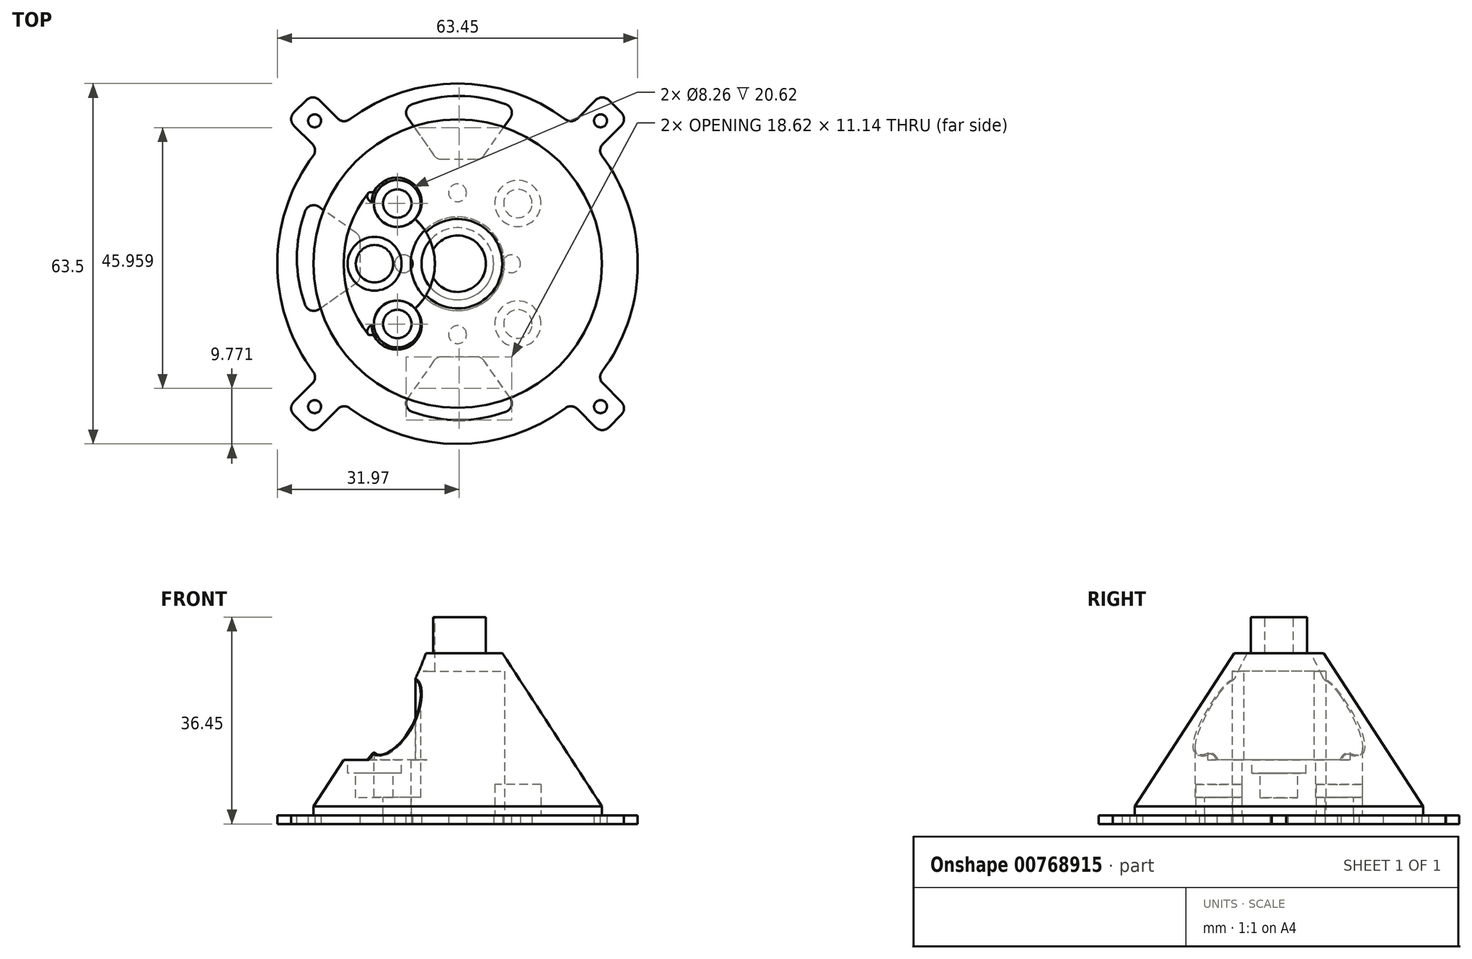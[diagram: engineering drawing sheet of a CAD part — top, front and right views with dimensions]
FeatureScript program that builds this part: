
annotation { "Feature Type Name" : "Feature", "Feature Type Description" : "" }
export const myFeature = defineFeature(function(context is Context, id is Id, definition is map)
    precondition{}
    {
        {
            var Q0;
            Q0=qCreatedBy(makeId("Top.planeOp"),FACE);
            var sketch = newSketch(context, id + "F0", { "sketchPlane" : qUnion([Q0])});
            skCircle(sketch, "E0", {"center": v(-0.25, -1) * mm, "radius": 6.35 * mm});
            skArc(sketch, "E1", {"start": v(-31.97, -2.27) * mm, "mid": v(-0.25, -32.75) * mm, "end": v(31.48, -2.27) * mm});
            skArc(sketch, "E2", {"start": v(-66.24, 8.52) * mm, "mid": v(-66.7, 4.4) * mm, "end": v(-66.91, 0.27) * mm});
            skArc(sketch, "E3", {"start": v(-82.25, 8.52) * mm, "mid": v(-82.8, -1) * mm, "end": v(-82.25, -10.53) * mm});
            skCircle(sketch, "E4", {"center": v(-0.25, -1) * mm, "radius": 15.01 * mm, "construction": true});
            skLineSegment(sketch, "E5", {"start": v(-0.25, -1) * mm, "end": v(-82.8, -1) * mm, "construction": true});
            skLineSegment(sketch, "E6", {"start": v(-0.25, -1) * mm, "end": v(82.3, -1) * mm, "construction": true});
            skLineSegment(sketch, "E7", {"start": v(-66.91, 0.27) * mm, "end": v(-31.97, 0.27) * mm});
            skLineSegment(sketch, "E8", {"start": v(-66.91, -2.27) * mm, "end": v(-31.97, -2.27) * mm});
            skLineSegment(sketch, "E9", {"start": v(-82.25, 8.52) * mm, "end": v(-66.24, 8.52) * mm});
            skLineSegment(sketch, "E10", {"start": v(-82.25, -10.53) * mm, "end": v(-66.24, -10.53) * mm});
            skLineSegment(sketch, "E11", {"start": v(31.48, 0.27) * mm, "end": v(66.41, 0.27) * mm});
            skLineSegment(sketch, "E12", {"start": v(31.48, -2.27) * mm, "end": v(66.41, -2.27) * mm});
            skLineSegment(sketch, "E13", {"start": v(65.74, 8.52) * mm, "end": v(81.75, 8.52) * mm});
            skLineSegment(sketch, "E14", {"start": v(65.74, -10.53) * mm, "end": v(81.75, -10.53) * mm});
            skLineSegment(sketch, "E15", {"start": v(-0.25, -1) * mm, "end": v(-0.25, 65.67) * mm, "construction": true});
            skCircle(sketch, "E16", {"center": v(-10.86, 9.61) * mm, "radius": 2.5 * mm});
            skCircle(sketch, "E17", {"center": v(10.37, 9.61) * mm, "radius": 2.5 * mm});
            skCircle(sketch, "E18", {"center": v(-10.86, -11.62) * mm, "radius": 2.5 * mm});
            skCircle(sketch, "E19", {"center": v(10.37, -11.62) * mm, "radius": 2.5 * mm});
            skLineSegment(sketch, "E20", {"start": v(-27.98, 26.72) * mm, "end": v(10.37, -11.62) * mm, "construction": true});
            skLineSegment(sketch, "E21", {"start": v(10.37, 9.61) * mm, "end": v(-10.86, -11.62) * mm, "construction": true});
            skArc(sketch, "E22.trimOffspring", {"start": v(81.75, -10.53) * mm, "mid": v(82.3, -1) * mm, "end": v(81.75, 8.52) * mm});
            skArc(sketch, "E23.trimOffspring", {"start": v(65.74, -10.53) * mm, "mid": v(66.2, -6.41) * mm, "end": v(66.41, -2.27) * mm});
            skArc(sketch, "E24.trimOffspring", {"start": v(-66.24, -10.53) * mm, "mid": v(66.25, 3.77) * mm, "end": v(-66.92, -1) * mm, "construction": true});
            skArc(sketch, "E25.trimOffspring", {"start": v(-66.91, -2.27) * mm, "mid": v(-66.7, -6.41) * mm, "end": v(-66.24, -10.53) * mm});
            skArc(sketch, "E26.trimOffspring", {"start": v(31.48, 0.27) * mm, "mid": v(-0.25, 30.75) * mm, "end": v(-31.97, 0.27) * mm});
            skArc(sketch, "E27.trimOffspring", {"start": v(66.43, -1) * mm, "mid": v(66.25, 3.77) * mm, "end": v(65.74, 8.52) * mm, "construction": true});
            skArc(sketch, "E28.trimOffspring", {"start": v(66.41, 0.27) * mm, "mid": v(66.2, 4.4) * mm, "end": v(65.74, 8.52) * mm});
            skArc(sketch, "E29", {"start": v(-31.97, -2.27) * mm, "mid": v(-32, -1) * mm, "end": v(-31.97, 0.27) * mm});
            skArc(sketch, "E30", {"start": v(31.48, -2.27) * mm, "mid": v(31.5, -1) * mm, "end": v(31.48, 0.27) * mm});
            skCircle(sketch, "E31", {"center": v(-76.45, -1) * mm, "radius": 3.24 * mm});
            skCircle(sketch, "E32.MirrorC", {"center": v(75.95, -1) * mm, "radius": 3.24 * mm});
            skCircle(sketch, "E33", {"center": v(-9.75, -1) * mm, "radius": 1.57 * mm});
            skCircle(sketch, "E34", {"center": v(9.25, -1) * mm, "radius": 1.57 * mm});
            skCircle(sketch, "E35", {"center": v(-0.25, 11.5) * mm, "radius": 1.57 * mm});
            skCircle(sketch, "E36", {"center": v(-0.25, -13.5) * mm, "radius": 1.57 * mm});
            skCircle(sketch, "E37", {"center": v(-0.25, -1) * mm, "radius": 9.5 * mm, "construction": true});
            skCircle(sketch, "E38", {"center": v(-0.25, -1) * mm, "radius": 12.5 * mm, "construction": true});
            skLineSegment(sketch, "E39", {"start": v(-66.91, 0.27) * mm, "end": v(-66.91, -2.27) * mm});
            skLineSegment(sketch, "E40", {"start": v(66.41, 0.27) * mm, "end": v(66.41, -2.27) * mm});
            skLineSegment(sketch, "E41.bottom", {"start": v(-31.97, -2.27) * mm, "end": v(-62.47, -2.27) * mm});
            skLineSegment(sketch, "E41.top", {"start": v(-31.97, 0.27) * mm, "end": v(-62.47, 0.27) * mm});
            skLineSegment(sketch, "E41.right", {"start": v(-62.47, -2.27) * mm, "end": v(-62.47, 0.27) * mm});
            skLineSegment(sketch, "E42.bottom", {"start": v(31.48, -2.27) * mm, "end": v(61.97, -2.27) * mm});
            skLineSegment(sketch, "E42.top", {"start": v(31.48, 0.27) * mm, "end": v(61.97, 0.27) * mm});
            skLineSegment(sketch, "E42.right", {"start": v(61.97, -2.27) * mm, "end": v(61.97, 0.27) * mm});
            skCircle(sketch, "E43", {"center": v(-0.25, -1) * mm, "radius": 62.23 * mm, "construction": true});
            skLineSegment(sketch, "E44.bottom", {"start": v(-31.97, 0.27) * mm, "end": v(-28.8, 0.27) * mm});
            skLineSegment(sketch, "E44.top", {"start": v(-31.97, -2.27) * mm, "end": v(-28.8, -2.27) * mm});
            skLineSegment(sketch, "E44.left", {"start": v(-31.97, 0.27) * mm, "end": v(-31.97, -2.27) * mm});
            skLineSegment(sketch, "E44.right", {"start": v(-28.8, 0.27) * mm, "end": v(-28.8, -2.27) * mm});
            skLineSegment(sketch, "E45.bottom", {"start": v(31.48, 0.27) * mm, "end": v(28.3, 0.27) * mm});
            skLineSegment(sketch, "E45.top", {"start": v(31.48, -2.27) * mm, "end": v(28.3, -2.27) * mm});
            skLineSegment(sketch, "E45.left", {"start": v(31.48, 0.27) * mm, "end": v(31.48, -2.27) * mm});
            skLineSegment(sketch, "E45.right", {"start": v(28.3, 0.27) * mm, "end": v(28.3, -2.27) * mm});
            skLineSegment(sketch, "E46", {"start": v(-20.34, 23.58) * mm, "end": v(-25.73, 28.97) * mm});
            skLineSegment(sketch, "E47", {"start": v(-25.73, 28.97) * mm, "end": v(-30.22, 24.48) * mm});
            skLineSegment(sketch, "E48", {"start": v(-30.22, 24.48) * mm, "end": v(-24.83, 19.09) * mm});
            skCircle(sketch, "E49", {"center": v(-25.43, 24.17) * mm, "radius": 1.14 * mm});
            skPoint(sketch, "E50.center", {"position": v(0, 0) * mm});
            skLineSegment(sketch, "E51.1.0", {"start": v(-25.73, -30.98) * mm, "end": v(-20.34, -25.59) * mm});
            skLineSegment(sketch, "E51.1.1", {"start": v(-24.83, -21.1) * mm, "end": v(-30.22, -26.49) * mm});
            skLineSegment(sketch, "E51.1.2", {"start": v(-30.22, -26.49) * mm, "end": v(-25.73, -30.98) * mm});
            skCircle(sketch, "E51.1.3", {"center": v(-25.43, -26.18) * mm, "radius": 1.14 * mm});
            skLineSegment(sketch, "E51.2.0", {"start": v(29.72, -26.49) * mm, "end": v(24.33, -21.1) * mm});
            skLineSegment(sketch, "E51.2.1", {"start": v(19.84, -25.59) * mm, "end": v(25.23, -30.98) * mm});
            skLineSegment(sketch, "E51.2.2", {"start": v(25.23, -30.98) * mm, "end": v(29.72, -26.49) * mm});
            skCircle(sketch, "E51.2.3", {"center": v(24.93, -26.18) * mm, "radius": 1.14 * mm});
            skLineSegment(sketch, "E51.3.0", {"start": v(25.23, 28.97) * mm, "end": v(19.84, 23.58) * mm});
            skLineSegment(sketch, "E51.3.1", {"start": v(24.33, 19.09) * mm, "end": v(29.72, 24.48) * mm});
            skLineSegment(sketch, "E51.3.2", {"start": v(29.72, 24.48) * mm, "end": v(25.23, 28.97) * mm});
            skCircle(sketch, "E51.3.3", {"center": v(24.93, 24.17) * mm, "radius": 1.14 * mm});
            skSolve(sketch);
        }
        {
            var Q0;
            Q0=makeQuery(id+"F0.imprint","IMPRINT",FACE,{"disambiguationData":[TD([[makeQuery(id+"F0.imprint","IMPRINT",EDGE,{"derivedFrom":sQuery(id+"F0.wireOp",EDGE,"E0")}),-1.0]])]});
            var Q1;
            Q1=makeQuery(id+"F0.imprint","IMPRINT",FACE,{"disambiguationData":[TD([[makeQuery(id+"F0.imprint","IMPRINT",EDGE,{"derivedFrom":sQuery(id+"F0.wireOp",EDGE,"E44.bottom")}),-1.0]])]});
            var Q2;
            Q2=makeQuery(id+"F0.imprint","IMPRINT",FACE,{"disambiguationData":[TD([[makeQuery(id+"F0.imprint","IMPRINT",EDGE,{"derivedFrom":sQuery(id+"F0.wireOp",EDGE,"E45.bottom")}),1.0]])]});
            var Q3;
            {var subQ1=sQuery(id+"F0.wireOp",EDGE,"E46");Q3=makeQuery(id+"F0.imprint","IMPRINT",FACE,{"disambiguationData":[TD([[makeQuery(id+"F0.imprint","IMPRINT",EDGE,{"derivedFrom":subQ1}),1.0]])]});}
            var Q4;
            {var subQ1=sQuery(id+"F0.wireOp",EDGE,"E51.3.0");Q4=makeQuery(id+"F0.imprint","IMPRINT",FACE,{"disambiguationData":[TD([[makeQuery(id+"F0.imprint","IMPRINT",EDGE,{"derivedFrom":subQ1}),1.0]])]});}
            var Q5;
            {var subQ1=sQuery(id+"F0.wireOp",EDGE,"E51.2.0");Q5=makeQuery(id+"F0.imprint","IMPRINT",FACE,{"disambiguationData":[TD([[makeQuery(id+"F0.imprint","IMPRINT",EDGE,{"derivedFrom":subQ1}),1.0]])]});}
            var Q6;
            {var subQ1=sQuery(id+"F0.wireOp",EDGE,"E51.1.0");Q6=makeQuery(id+"F0.imprint","IMPRINT",FACE,{"disambiguationData":[TD([[makeQuery(id+"F0.imprint","IMPRINT",EDGE,{"derivedFrom":subQ1}),1.0]])]});}
            extrude(context, id + "F1", {"entities" : qUnion([Q0, Q1, Q2, Q3, Q4, Q5, Q6]), "depth" : 1.52 * mm, "offsetDistance" : 25.4 * mm});
        }
        {
            var Q0;
            Q0=makeQuery(id+"F1.opExtrude","CAP_FACE",FACE,{"disambiguationData":[OSD([sQuery(id+"F0.wireOp",EDGE,"E0"),sQuery(id+"F0.wireOp",EDGE,"E1"),sQuery(id+"F0.wireOp",EDGE,"E16"),sQuery(id+"F0.wireOp",EDGE,"E17"),sQuery(id+"F0.wireOp",EDGE,"E18"),sQuery(id+"F0.wireOp",EDGE,"E19"),sQuery(id+"F0.wireOp",EDGE,"E26.trimOffspring"),sQuery(id+"F0.wireOp",EDGE,"E33"),sQuery(id+"F0.wireOp",EDGE,"E34"),sQuery(id+"F0.wireOp",EDGE,"E35"),sQuery(id+"F0.wireOp",EDGE,"E36"),sQuery(id+"F0.wireOp",EDGE,"E44.left"),sQuery(id+"F0.wireOp",EDGE,"E45.left")])],"isStart":false});
            var sketch = newSketch(context, id + "F2", { "sketchPlane" : qUnion([Q0])});
            skLineSegment(sketch, "E52", {"start": v(-4.4, -18.09) * mm, "end": v(-9.03, -24.68) * mm});
            skLineSegment(sketch, "E53", {"start": v(9.03, -24.68) * mm, "end": v(4.4, -18.09) * mm});
            skLineSegment(sketch, "E54", {"start": v(3.1, -17.41) * mm, "end": v(-3.1, -17.41) * mm});
            skArc(sketch, "E55", {"start": v(-8.27, -27.08) * mm, "mid": v(0, -28.55) * mm, "end": v(8.27, -27.08) * mm});
            skPoint(sketch, "E56.visualSharp", {"position": v(-3.94, -17.41) * mm});
            skArc(sketch, "E56.filletArc", {"start": v(-3.1, -17.41) * mm, "mid": v(-3.84, -17.59) * mm, "end": v(-4.4, -18.09) * mm});
            skPoint(sketch, "E57.visualSharp", {"position": v(-10.16, -26.3) * mm});
            skArc(sketch, "E57.filletArc", {"start": v(-9.03, -24.68) * mm, "mid": v(-9.24, -26.07) * mm, "end": v(-8.27, -27.08) * mm});
            skPoint(sketch, "E58.visualSharp", {"position": v(10.16, -26.3) * mm});
            skArc(sketch, "E58.filletArc", {"start": v(8.27, -27.08) * mm, "mid": v(9.24, -26.07) * mm, "end": v(9.03, -24.68) * mm});
            skPoint(sketch, "E59.visualSharp", {"position": v(3.94, -17.41) * mm});
            skArc(sketch, "E59.filletArc", {"start": v(4.4, -18.09) * mm, "mid": v(3.84, -17.59) * mm, "end": v(3.1, -17.41) * mm});
            skPoint(sketch, "E60.1.0", {"position": v(-17.41, 3.94) * mm});
            skLineSegment(sketch, "E60.1.1", {"start": v(-17.41, -3.1) * mm, "end": v(-17.41, 3.1) * mm});
            skArc(sketch, "E60.1.2", {"start": v(-27.08, 8.27) * mm, "mid": v(-28.55, 0) * mm, "end": v(-27.08, -8.27) * mm});
            skPoint(sketch, "E60.1.3", {"position": v(-26.3, 10.16) * mm});
            skLineSegment(sketch, "E60.1.4", {"start": v(-24.68, -9.03) * mm, "end": v(-18.09, -4.4) * mm});
            skPoint(sketch, "E60.1.5", {"position": v(-26.3, -10.16) * mm});
            skPoint(sketch, "E60.1.6", {"position": v(-17.41, -3.94) * mm});
            skLineSegment(sketch, "E60.1.7", {"start": v(-18.09, 4.4) * mm, "end": v(-24.68, 9.03) * mm});
            skArc(sketch, "E60.1.8", {"start": v(-27.08, -8.27) * mm, "mid": v(-26.07, -9.24) * mm, "end": v(-24.68, -9.03) * mm});
            skArc(sketch, "E60.1.9", {"start": v(-24.68, 9.03) * mm, "mid": v(-26.07, 9.24) * mm, "end": v(-27.08, 8.27) * mm});
            skArc(sketch, "E60.1.10", {"start": v(-18.09, -4.4) * mm, "mid": v(-17.59, -3.84) * mm, "end": v(-17.41, -3.1) * mm});
            skArc(sketch, "E60.1.11", {"start": v(-17.41, 3.1) * mm, "mid": v(-17.59, 3.84) * mm, "end": v(-18.09, 4.4) * mm});
            skPoint(sketch, "E60.2.0", {"position": v(3.94, 17.41) * mm});
            skLineSegment(sketch, "E60.2.1", {"start": v(-3.1, 17.41) * mm, "end": v(3.1, 17.41) * mm});
            skArc(sketch, "E60.2.2", {"start": v(8.27, 27.08) * mm, "mid": v(0, 28.55) * mm, "end": v(-8.27, 27.08) * mm});
            skPoint(sketch, "E60.2.3", {"position": v(10.16, 26.3) * mm});
            skLineSegment(sketch, "E60.2.4", {"start": v(-9.03, 24.68) * mm, "end": v(-4.4, 18.09) * mm});
            skPoint(sketch, "E60.2.5", {"position": v(-10.16, 26.3) * mm});
            skPoint(sketch, "E60.2.6", {"position": v(-3.94, 17.41) * mm});
            skLineSegment(sketch, "E60.2.7", {"start": v(4.4, 18.09) * mm, "end": v(9.03, 24.68) * mm});
            skArc(sketch, "E60.2.8", {"start": v(-8.27, 27.08) * mm, "mid": v(-9.24, 26.07) * mm, "end": v(-9.03, 24.68) * mm});
            skArc(sketch, "E60.2.9", {"start": v(9.03, 24.68) * mm, "mid": v(9.24, 26.07) * mm, "end": v(8.27, 27.08) * mm});
            skArc(sketch, "E60.2.10", {"start": v(-4.4, 18.09) * mm, "mid": v(-3.84, 17.59) * mm, "end": v(-3.1, 17.41) * mm});
            skArc(sketch, "E60.2.11", {"start": v(3.1, 17.41) * mm, "mid": v(3.84, 17.59) * mm, "end": v(4.4, 18.09) * mm});
            skPoint(sketch, "E60.center", {"position": v(0, 0) * mm});
            skLineSegment(sketch, "E60.anchor1", {"start": v(0, 0) * mm, "end": v(-10.16, -26.3) * mm, "construction": true});
            skLineSegment(sketch, "E60.anchor2", {"start": v(0, 0) * mm, "end": v(10.16, 26.3) * mm, "construction": true});
            skSolve(sketch);
        }
        {
            var Q0;
            Q0 = qSketchRegion(id + "F2", true);
            extrude(context, id + "F3", {"entities" : qUnion([Q0]), "operationType" : NewBodyOperationType.REMOVE, "endBound" : BoundingType.THROUGH_ALL, "oppositeDirection" : true, "depth" : 25.4 * mm, "offsetDistance" : 25.4 * mm});
        }
        {
            var Q0;
            Q0=makeQuery(id+"F1.opExtrude","SWEPT_EDGE",EDGE,{"disambiguationData":[OSD([sQuery(id+"F0.wireOp",EDGE,"E26.trimOffspring"),sQuery(id+"F0.wireOp",EDGE,"E48")])]});
            var Q1;
            Q1=makeQuery(id+"F1.opExtrude","SWEPT_EDGE",EDGE,{"disambiguationData":[OSD([sQuery(id+"F0.wireOp",EDGE,"E47"),sQuery(id+"F0.wireOp",EDGE,"E48")])]});
            var Q2;
            Q2=makeQuery(id+"F1.opExtrude","SWEPT_EDGE",EDGE,{"disambiguationData":[OSD([sQuery(id+"F0.wireOp",EDGE,"E46"),sQuery(id+"F0.wireOp",EDGE,"E47")])]});
            var Q3;
            Q3=makeQuery(id+"F1.opExtrude","SWEPT_EDGE",EDGE,{"disambiguationData":[OSD([sQuery(id+"F0.wireOp",EDGE,"E26.trimOffspring"),sQuery(id+"F0.wireOp",EDGE,"E46")])]});
            var Q4;
            Q4=makeQuery(id+"F1.opExtrude","SWEPT_EDGE",EDGE,{"disambiguationData":[OSD([sQuery(id+"F0.wireOp",EDGE,"E26.trimOffspring"),sQuery(id+"F0.wireOp",EDGE,"E51.3.0")])]});
            var Q5;
            Q5=makeQuery(id+"F1.opExtrude","SWEPT_EDGE",EDGE,{"disambiguationData":[OSD([sQuery(id+"F0.wireOp",EDGE,"E51.3.0"),sQuery(id+"F0.wireOp",EDGE,"E51.3.2")])]});
            var Q6;
            Q6=makeQuery(id+"F1.opExtrude","SWEPT_EDGE",EDGE,{"disambiguationData":[OSD([sQuery(id+"F0.wireOp",EDGE,"E51.3.1"),sQuery(id+"F0.wireOp",EDGE,"E51.3.2")])]});
            var Q7;
            Q7=makeQuery(id+"F1.opExtrude","SWEPT_EDGE",EDGE,{"disambiguationData":[OSD([sQuery(id+"F0.wireOp",EDGE,"E26.trimOffspring"),sQuery(id+"F0.wireOp",EDGE,"E51.3.1")])]});
            var Q8;
            Q8=makeQuery(id+"F1.opExtrude","SWEPT_EDGE",EDGE,{"disambiguationData":[OSD([sQuery(id+"F0.wireOp",EDGE,"E1"),sQuery(id+"F0.wireOp",EDGE,"E51.2.0")])]});
            var Q9;
            Q9=makeQuery(id+"F1.opExtrude","SWEPT_EDGE",EDGE,{"disambiguationData":[OSD([sQuery(id+"F0.wireOp",EDGE,"E51.2.0"),sQuery(id+"F0.wireOp",EDGE,"E51.2.2")])]});
            var Q10;
            Q10=makeQuery(id+"F1.opExtrude","SWEPT_EDGE",EDGE,{"disambiguationData":[OSD([sQuery(id+"F0.wireOp",EDGE,"E51.2.1"),sQuery(id+"F0.wireOp",EDGE,"E51.2.2")])]});
            var Q11;
            Q11=makeQuery(id+"F1.opExtrude","SWEPT_EDGE",EDGE,{"disambiguationData":[OSD([sQuery(id+"F0.wireOp",EDGE,"E1"),sQuery(id+"F0.wireOp",EDGE,"E51.2.1")])]});
            var Q12;
            Q12=makeQuery(id+"F1.opExtrude","SWEPT_EDGE",EDGE,{"disambiguationData":[OSD([sQuery(id+"F0.wireOp",EDGE,"E1"),sQuery(id+"F0.wireOp",EDGE,"E51.1.0")])]});
            var Q13;
            Q13=makeQuery(id+"F1.opExtrude","SWEPT_EDGE",EDGE,{"disambiguationData":[OSD([sQuery(id+"F0.wireOp",EDGE,"E51.1.0"),sQuery(id+"F0.wireOp",EDGE,"E51.1.2")])]});
            var Q14;
            Q14=makeQuery(id+"F1.opExtrude","SWEPT_EDGE",EDGE,{"disambiguationData":[OSD([sQuery(id+"F0.wireOp",EDGE,"E51.1.1"),sQuery(id+"F0.wireOp",EDGE,"E51.1.2")])]});
            var Q15;
            Q15=makeQuery(id+"F1.opExtrude","SWEPT_EDGE",EDGE,{"disambiguationData":[OSD([sQuery(id+"F0.wireOp",EDGE,"E1"),sQuery(id+"F0.wireOp",EDGE,"E51.1.1")])]});
            fillet(context, id + "F4", {"entities" : qUnion([Q0, Q1, Q2, Q3, Q4, Q5, Q6, Q7, Q8, Q9, Q10, Q11, Q12, Q13, Q14, Q15]), "radius" : 1.59 * mm, "tangentPropagation" : true, "allowEdgeOverflow" : false});
        }
        {
            var Q0;
            Q0=makeQuery(id+"F1.opExtrude","CAP_FACE",FACE,{"disambiguationData":[OSD([sQuery(id+"F0.wireOp",EDGE,"E0"),sQuery(id+"F0.wireOp",EDGE,"E1"),sQuery(id+"F0.wireOp",EDGE,"E16"),sQuery(id+"F0.wireOp",EDGE,"E17"),sQuery(id+"F0.wireOp",EDGE,"E18"),sQuery(id+"F0.wireOp",EDGE,"E19"),sQuery(id+"F0.wireOp",EDGE,"E26.trimOffspring"),sQuery(id+"F0.wireOp",EDGE,"E33"),sQuery(id+"F0.wireOp",EDGE,"E34"),sQuery(id+"F0.wireOp",EDGE,"E35"),sQuery(id+"F0.wireOp",EDGE,"E36"),sQuery(id+"F0.wireOp",EDGE,"E44.left"),sQuery(id+"F0.wireOp",EDGE,"E45.left"),sQuery(id+"F0.wireOp",EDGE,"E46"),sQuery(id+"F0.wireOp",EDGE,"E47"),sQuery(id+"F0.wireOp",EDGE,"E48"),sQuery(id+"F0.wireOp",EDGE,"E49"),sQuery(id+"F0.wireOp",EDGE,"E51.1.0"),sQuery(id+"F0.wireOp",EDGE,"E51.1.1"),sQuery(id+"F0.wireOp",EDGE,"E51.1.2"),sQuery(id+"F0.wireOp",EDGE,"E51.1.3"),sQuery(id+"F0.wireOp",EDGE,"E51.2.0"),sQuery(id+"F0.wireOp",EDGE,"E51.2.1"),sQuery(id+"F0.wireOp",EDGE,"E51.2.2"),sQuery(id+"F0.wireOp",EDGE,"E51.2.3"),sQuery(id+"F0.wireOp",EDGE,"E51.3.0"),sQuery(id+"F0.wireOp",EDGE,"E51.3.1"),sQuery(id+"F0.wireOp",EDGE,"E51.3.2"),sQuery(id+"F0.wireOp",EDGE,"E51.3.3")])],"isStart":false});
            var sketch = newSketch(context, id + "F5", { "sketchPlane" : qUnion([Q0])});
            skCircle(sketch, "E61", {"center": v(-0.25, -1) * mm, "radius": 25.4 * mm});
            skSolve(sketch);
        }
        {
            var Q0;
            Q0 = qSketchRegion(id + "F5", true);
            extrude(context, id + "F6", {"entities" : qUnion([Q0]), "depth" : 1.59 * mm, "offsetDistance" : 25.4 * mm});
        }
        {
            var Q0;
            Q0=makeQuery(id+"F6.opExtrude","CAP_FACE",FACE,{"disambiguationData":[OSD([sQuery(id+"F5.wireOp",EDGE,"E61")])],"isStart":false});
            extrude(context, id + "F7", {"entities" : qUnion([Q0]), "operationType" : NewBodyOperationType.ADD, "depth" : 26.99 * mm, "offsetDistance" : 25.4 * mm, "hasDraft" : true, "draftAngle" : 33 * degree, "draftPullDirection" : true});
        }
        {
            var Q0;
            Q0=makeQuery(id+"F7.opExtrude","CAP_FACE",FACE,{"disambiguationData":[OSD([sQuery(id+"F5.wireOp",EDGE,"E61")])],"isStart":false});
            var sketch = newSketch(context, id + "F8", { "sketchPlane" : qUnion([Q0])});
            skCircle(sketch, "E62", {"center": v(-0.25, -1) * mm, "radius": 4.98 * mm});
            skSolve(sketch);
        }
        {
            var Q0;
            Q0=makeQuery(id+"F8.imprint","IMPRINT",FACE,{"disambiguationData":[TD([[makeQuery(id+"F8.imprint","IMPRINT",EDGE,{"derivedFrom":sQuery(id+"F8.wireOp",EDGE,"E62")}),1.0]])]});
            extrude(context, id + "F9", {"entities" : qUnion([Q0]), "operationType" : NewBodyOperationType.ADD, "depth" : 6.35 * mm, "offsetDistance" : 25.4 * mm});
        }
        {
            var Q0;
            Q0=makeQuery(id+"F6.opExtrude","CAP_FACE",FACE,{"disambiguationData":[OSD([sQuery(id+"F5.wireOp",EDGE,"E61")])],"isStart":true});
            var sketch = newSketch(context, id + "F10", { "sketchPlane" : qUnion([Q0])});
            skCircle(sketch, "E63", {"center": v(-0.25, 1) * mm, "radius": 8.26 * mm});
            skSolve(sketch);
        }
        {
            var Q0;
            Q0 = qSketchRegion(id + "F10", true);
            extrude(context, id + "F11", {"entities" : qUnion([Q0]), "operationType" : NewBodyOperationType.REMOVE, "oppositeDirection" : true, "depth" : 25.4 * mm, "offsetDistance" : 25.4 * mm});
        }
        {
            var Q0;
            Q0=makeQuery(id+"F7.opExtrude","CAP_FACE",FACE,{"disambiguationData":[OSD([sQuery(id+"F5.wireOp",EDGE,"E61")])],"isStart":false});
            var sketch = newSketch(context, id + "F12", { "sketchPlane" : qUnion([Q0])});
            skCircle(sketch, "E64", {"center": v(-14.87, -1) * mm, "radius": 10.63 * mm});
            skSolve(sketch);
        }
        {
            var Q0;
            Q0 = qSketchRegion(id + "F12", true);
            extrude(context, id + "F13", {"entities" : qUnion([Q0]), "operationType" : NewBodyOperationType.REMOVE, "oppositeDirection" : true, "depth" : 18.8 * mm, "offsetDistance" : 25.4 * mm, "hasSecondDirection" : true, "secondDirectionOppositeDirection" : false, "secondDirectionDepth" : 25.4 * mm});
        }
        {
            var Q0;
            Q0=makeQuery(id+"F13.boolean.opBoolean","COPY",FACE,{"derivedFrom":makeQuery(id+"F13.opExtrude","CAP_FACE",FACE,{"disambiguationData":[OSD([sQuery(id+"F5.wireOp",EDGE,"E61"),sQuery(id+"F12.wireOp",EDGE,"E64")])],"isStart":false})});
            var sketch = newSketch(context, id + "F14", { "sketchPlane" : qUnion([Q0])});
            skCircle(sketch, "E65", {"center": v(-14.87, -1) * mm, "radius": 4.74 * mm});
            skSolve(sketch);
        }
        {
            var Q0;
            Q0=makeQuery(id+"F14.imprint","IMPRINT",FACE,{"disambiguationData":[TD([[makeQuery(id+"F14.imprint","IMPRINT",EDGE,{"derivedFrom":sQuery(id+"F14.wireOp",EDGE,"E65")}),1.0]])]});
            extrude(context, id + "F15", {"entities" : qUnion([Q0]), "operationType" : NewBodyOperationType.REMOVE, "oppositeDirection" : true, "depth" : 2.38 * mm, "offsetDistance" : 25.4 * mm});
        }
        {
            var Q0;
            Q0=makeQuery(id+"F15.boolean.opBoolean","COPY",FACE,{"derivedFrom":makeQuery(id+"F15.opExtrude","CAP_FACE",FACE,{"disambiguationData":[OSD([sQuery(id+"F14.wireOp",EDGE,"E65")])],"isStart":false})});
            var sketch = newSketch(context, id + "F16", { "sketchPlane" : qUnion([Q0])});
            skCircle(sketch, "E66", {"center": v(-14.87, -1) * mm, "radius": 3.3 * mm});
            skSolve(sketch);
        }
        {
            var Q0;
            Q0=makeQuery(id+"F16.imprint","IMPRINT",FACE,{"disambiguationData":[TD([[makeQuery(id+"F16.imprint","IMPRINT",EDGE,{"derivedFrom":sQuery(id+"F16.wireOp",EDGE,"E66")}),1.0]])]});
            extrude(context, id + "F17", {"entities" : qUnion([Q0]), "operationType" : NewBodyOperationType.REMOVE, "oppositeDirection" : true, "depth" : 4.32 * mm, "offsetDistance" : 25.4 * mm});
        }
        {
            var Q0;
            Q0=makeQuery(id+"F1.opExtrude","CAP_FACE",FACE,{"disambiguationData":[OSD([sQuery(id+"F0.wireOp",EDGE,"E0"),sQuery(id+"F0.wireOp",EDGE,"E1"),sQuery(id+"F0.wireOp",EDGE,"E16"),sQuery(id+"F0.wireOp",EDGE,"E17"),sQuery(id+"F0.wireOp",EDGE,"E18"),sQuery(id+"F0.wireOp",EDGE,"E19"),sQuery(id+"F0.wireOp",EDGE,"E26.trimOffspring"),sQuery(id+"F0.wireOp",EDGE,"E33"),sQuery(id+"F0.wireOp",EDGE,"E34"),sQuery(id+"F0.wireOp",EDGE,"E35"),sQuery(id+"F0.wireOp",EDGE,"E36"),sQuery(id+"F0.wireOp",EDGE,"E44.left"),sQuery(id+"F0.wireOp",EDGE,"E45.left"),sQuery(id+"F0.wireOp",EDGE,"E46"),sQuery(id+"F0.wireOp",EDGE,"E47"),sQuery(id+"F0.wireOp",EDGE,"E48"),sQuery(id+"F0.wireOp",EDGE,"E49"),sQuery(id+"F0.wireOp",EDGE,"E51.1.0"),sQuery(id+"F0.wireOp",EDGE,"E51.1.1"),sQuery(id+"F0.wireOp",EDGE,"E51.1.2"),sQuery(id+"F0.wireOp",EDGE,"E51.1.3"),sQuery(id+"F0.wireOp",EDGE,"E51.2.0"),sQuery(id+"F0.wireOp",EDGE,"E51.2.1"),sQuery(id+"F0.wireOp",EDGE,"E51.2.2"),sQuery(id+"F0.wireOp",EDGE,"E51.2.3"),sQuery(id+"F0.wireOp",EDGE,"E51.3.0"),sQuery(id+"F0.wireOp",EDGE,"E51.3.1"),sQuery(id+"F0.wireOp",EDGE,"E51.3.2"),sQuery(id+"F0.wireOp",EDGE,"E51.3.3")])],"isStart":false});
            var sketch = newSketch(context, id + "F18", { "sketchPlane" : qUnion([Q0])});
            skCircle(sketch, "E67", {"center": v(10.37, -11.62) * mm, "radius": 4.06 * mm});
            skCircle(sketch, "E68", {"center": v(10.37, 9.61) * mm, "radius": 4.06 * mm});
            skSolve(sketch);
        }
        {
            var Q0;
            Q0 = qSketchRegion(id + "F18", true);
            extrude(context, id + "F19", {"entities" : qUnion([Q0]), "operationType" : NewBodyOperationType.REMOVE, "depth" : 5.46 * mm, "offsetDistance" : 25.4 * mm});
        }
        {
            var Q0;
            Q0=makeQuery(id+"F7.opExtrude","CAP_FACE",FACE,{"disambiguationData":[OSD([sQuery(id+"F5.wireOp",EDGE,"E61")])],"isStart":false});
            var sketch = newSketch(context, id + "F20", { "sketchPlane" : qUnion([Q0])});
            skCircle(sketch, "E69", {"center": v(-10.86, -11.62) * mm, "radius": 4.13 * mm});
            skCircle(sketch, "E70", {"center": v(-10.86, 9.61) * mm, "radius": 4.13 * mm});
            skSolve(sketch);
        }
        {
            var Q0;
            Q0 = qSketchRegion(id + "F20", true);
            var Q1;
            Q1=makeQuery(id+"F1.opExtrude","CAP_FACE",FACE,{"disambiguationData":[OSD([sQuery(id+"F0.wireOp",EDGE,"E0"),sQuery(id+"F0.wireOp",EDGE,"E1"),sQuery(id+"F0.wireOp",EDGE,"E16"),sQuery(id+"F0.wireOp",EDGE,"E17"),sQuery(id+"F0.wireOp",EDGE,"E18"),sQuery(id+"F0.wireOp",EDGE,"E19"),sQuery(id+"F0.wireOp",EDGE,"E26.trimOffspring"),sQuery(id+"F0.wireOp",EDGE,"E33"),sQuery(id+"F0.wireOp",EDGE,"E34"),sQuery(id+"F0.wireOp",EDGE,"E35"),sQuery(id+"F0.wireOp",EDGE,"E36"),sQuery(id+"F0.wireOp",EDGE,"E44.left"),sQuery(id+"F0.wireOp",EDGE,"E45.left"),sQuery(id+"F0.wireOp",EDGE,"E46"),sQuery(id+"F0.wireOp",EDGE,"E47"),sQuery(id+"F0.wireOp",EDGE,"E48"),sQuery(id+"F0.wireOp",EDGE,"E49"),sQuery(id+"F0.wireOp",EDGE,"E51.1.0"),sQuery(id+"F0.wireOp",EDGE,"E51.1.1"),sQuery(id+"F0.wireOp",EDGE,"E51.1.2"),sQuery(id+"F0.wireOp",EDGE,"E51.1.3"),sQuery(id+"F0.wireOp",EDGE,"E51.2.0"),sQuery(id+"F0.wireOp",EDGE,"E51.2.1"),sQuery(id+"F0.wireOp",EDGE,"E51.2.2"),sQuery(id+"F0.wireOp",EDGE,"E51.2.3"),sQuery(id+"F0.wireOp",EDGE,"E51.3.0"),sQuery(id+"F0.wireOp",EDGE,"E51.3.1"),sQuery(id+"F0.wireOp",EDGE,"E51.3.2"),sQuery(id+"F0.wireOp",EDGE,"E51.3.3")])],"isStart":false});
            extrude(context, id + "F21", {"entities" : qUnion([Q0]), "operationType" : NewBodyOperationType.REMOVE, "endBound" : BoundingType.UP_TO_SURFACE, "oppositeDirection" : true, "depth" : 25.4 * mm, "endBoundEntityFace" : qUnion([Q1]), "hasOffset" : true, "offsetDistance" : 3.17 * mm});
        }
        {
            var Q0;
            Q0=makeQuery(id+"F21.boolean.opBoolean","COPY",FACE,{"derivedFrom":makeQuery(id+"F21.opExtrude","CAP_FACE",FACE,{"disambiguationData":[OSD([sQuery(id+"F20.wireOp",EDGE,"E70")])],"isStart":false})});
            var sketch = newSketch(context, id + "F22", { "sketchPlane" : qUnion([Q0])});
            skCircle(sketch, "E71.0", {"center": v(-10.86, 9.61) * mm, "radius": 2.5 * mm});
            skCircle(sketch, "E72.0", {"center": v(-10.86, -11.62) * mm, "radius": 2.5 * mm});
            skSolve(sketch);
        }
        {
            var Q0;
            Q0 = qSketchRegion(id + "F22", true);
            extrude(context, id + "F23", {"entities" : qUnion([Q0]), "operationType" : NewBodyOperationType.REMOVE, "endBound" : BoundingType.THROUGH_ALL, "oppositeDirection" : true, "depth" : 25.4 * mm, "offsetDistance" : 25.4 * mm});
        }
        {
            var Q0;
            Q0=makeQuery(id+"F13.boolean.opBoolean","INTERSECT",EDGE,{"disambiguationData":[OD(1.0)],"derivedFrom":[makeQuery(id+"F11.boolean.opBoolean","COPY",FACE,{"derivedFrom":makeQuery(id+"F11.opExtrude","SWEPT_FACE",FACE,{"disambiguationData":[OSD([sQuery(id+"F10.wireOp",EDGE,"E63")])]})}),makeQuery(id+"F13.opExtrude","SWEPT_FACE",FACE,{"disambiguationData":[OSD([sQuery(id+"F12.wireOp",EDGE,"E64")])]})]});
            var Q1;
            Q1=makeQuery(id+"F13.boolean.opBoolean","INTERSECT",EDGE,{"disambiguationData":[OD(0.0)],"derivedFrom":[makeQuery(id+"F11.boolean.opBoolean","COPY",FACE,{"derivedFrom":makeQuery(id+"F11.opExtrude","SWEPT_FACE",FACE,{"disambiguationData":[OSD([sQuery(id+"F10.wireOp",EDGE,"E63")])]})}),makeQuery(id+"F13.opExtrude","SWEPT_FACE",FACE,{"disambiguationData":[OSD([sQuery(id+"F12.wireOp",EDGE,"E64")])]})]});
            var Q2;
            Q2=makeQuery(id+"FgfgKUGcdIG3gcC_2.1.F13.boolean.opBoolean","INTERSECT",EDGE,{"disambiguationData":[OD(1.0)],"derivedFrom":[makeQuery(id+"F11.boolean.opBoolean","COPY",FACE,{"derivedFrom":makeQuery(id+"F11.opExtrude","SWEPT_FACE",FACE,{"disambiguationData":[OSD([sQuery(id+"F10.wireOp",EDGE,"E63")])]})}),makeQuery(id+"FgfgKUGcdIG3gcC_2.1.F13.opExtrude","SWEPT_FACE",FACE,{"disambiguationData":[OSD([sQuery(id+"F12.wireOp",EDGE,"E64")])]})]});
            var Q3;
            Q3=makeQuery(id+"FgfgKUGcdIG3gcC_2.1.F13.boolean.opBoolean","INTERSECT",EDGE,{"disambiguationData":[OD(0.0)],"derivedFrom":[makeQuery(id+"F11.boolean.opBoolean","COPY",FACE,{"derivedFrom":makeQuery(id+"F11.opExtrude","SWEPT_FACE",FACE,{"disambiguationData":[OSD([sQuery(id+"F10.wireOp",EDGE,"E63")])]})}),makeQuery(id+"FgfgKUGcdIG3gcC_2.1.F13.opExtrude","SWEPT_FACE",FACE,{"disambiguationData":[OSD([sQuery(id+"F12.wireOp",EDGE,"E64")])]})]});
            var Q4;
            Q4=makeQuery(id+"FgfgKUGcdIG3gcC_2.2.F13.boolean.opBoolean","INTERSECT",EDGE,{"disambiguationData":[OD(1.0)],"derivedFrom":[makeQuery(id+"F11.boolean.opBoolean","COPY",FACE,{"derivedFrom":makeQuery(id+"F11.opExtrude","SWEPT_FACE",FACE,{"disambiguationData":[OSD([sQuery(id+"F10.wireOp",EDGE,"E63")])]})}),makeQuery(id+"FgfgKUGcdIG3gcC_2.2.F13.opExtrude","SWEPT_FACE",FACE,{"disambiguationData":[OSD([sQuery(id+"F12.wireOp",EDGE,"E64")])]})]});
            var Q5;
            Q5=makeQuery(id+"FgfgKUGcdIG3gcC_2.2.F13.boolean.opBoolean","INTERSECT",EDGE,{"disambiguationData":[OD(0.0)],"derivedFrom":[makeQuery(id+"F11.boolean.opBoolean","COPY",FACE,{"derivedFrom":makeQuery(id+"F11.opExtrude","SWEPT_FACE",FACE,{"disambiguationData":[OSD([sQuery(id+"F10.wireOp",EDGE,"E63")])]})}),makeQuery(id+"FgfgKUGcdIG3gcC_2.2.F13.opExtrude","SWEPT_FACE",FACE,{"disambiguationData":[OSD([sQuery(id+"F12.wireOp",EDGE,"E64")])]})]});
            fillet(context, id + "F24", {"entities" : qUnion([Q0, Q1, Q2, Q3, Q4, Q5]), "radius" : 0.5 * mm, "tangentPropagation" : true, "allowEdgeOverflow" : false});
        }
        {
            var Q0;
            {var subQ0=makeQuery(id+"F7.opExtrude","SWEPT_FACE",FACE,{"disambiguationData":[OSD([sQuery(id+"F5.wireOp",EDGE,"E61")])]});var subQ1=sQuery(id+"F12.wireOp",EDGE,"E64");var subQ2=makeQuery(id+"F13.opExtrude","SWEPT_FACE",FACE,{"disambiguationData":[OSD([subQ1])]});Q0=makeQuery(id+"F21.boolean.opBoolean","SPLIT",EDGE,{"disambiguationData":[TD([makeQuery(id+"F13.boolean.opBoolean","COPY",FACE,{"derivedFrom":makeQuery(id+"F13.opExtrude","CAP_FACE",FACE,{"disambiguationData":[OSD([subQ1])],"isStart":false})})])],"derivedFrom":makeQuery(id+"F13.boolean.opBoolean","INTERSECT",EDGE,{"disambiguationData":[OD(1.0)],"derivedFrom":[subQ0,subQ2]})});}
            var Q1;
            {var subQ0=makeQuery(id+"F7.opExtrude","SWEPT_FACE",FACE,{"disambiguationData":[OSD([sQuery(id+"F5.wireOp",EDGE,"E61")])]});var subQ1=sQuery(id+"F12.wireOp",EDGE,"E64");var subQ2=makeQuery(id+"F13.opExtrude","SWEPT_FACE",FACE,{"disambiguationData":[OSD([subQ1])]});Q1=makeQuery(id+"F21.boolean.opBoolean","SPLIT",EDGE,{"disambiguationData":[TD([makeQuery(id+"F13.boolean.opBoolean","COPY",FACE,{"derivedFrom":makeQuery(id+"F13.opExtrude","CAP_FACE",FACE,{"disambiguationData":[OSD([subQ1])],"isStart":false})})])],"derivedFrom":makeQuery(id+"F13.boolean.opBoolean","INTERSECT",EDGE,{"disambiguationData":[OD(0.0)],"derivedFrom":[subQ0,subQ2]})});}
            fillet(context, id + "F25", {"entities" : qUnion([Q0, Q1]), "radius" : 1.27 * mm, "tangentPropagation" : true, "allowEdgeOverflow" : false});
        }
        {
            var Q0;
            {var subQ0=makeQuery(id+"F21.opExtrude","SWEPT_FACE",FACE,{"disambiguationData":[OSD([sQuery(id+"F20.wireOp",EDGE,"E70")])]});var subQ1=makeQuery(id+"F7.opExtrude","SWEPT_FACE",FACE,{"disambiguationData":[OSD([sQuery(id+"F5.wireOp",EDGE,"E61")])]});var subQ2=sQuery(id+"F12.wireOp",EDGE,"E64");var subQ3=makeQuery(id+"F13.opExtrude","SWEPT_FACE",FACE,{"disambiguationData":[OSD([subQ2])]});Q0=makeQuery(id+"F25.opFillet","BLEND_EDGE",EDGE,{"blendedFrom":[makeQuery(id+"F21.boolean.opBoolean","SPLIT",EDGE,{"disambiguationData":[TD([makeQuery(id+"F13.boolean.opBoolean","COPY",FACE,{"derivedFrom":makeQuery(id+"F13.opExtrude","CAP_FACE",FACE,{"disambiguationData":[OSD([subQ2])],"isStart":false})})])],"derivedFrom":makeQuery(id+"F13.boolean.opBoolean","INTERSECT",EDGE,{"disambiguationData":[OD(1.0)],"derivedFrom":[subQ1,subQ3]})}),makeQuery(id+"F21.boolean.opBoolean","COPY",FACE,{"derivedFrom":subQ0})],"blendedInto":[makeQuery(id+"F21.boolean.opBoolean","COPY",FACE,{"derivedFrom":subQ0})]});}
            var Q1;
            {var subQ0=makeQuery(id+"F21.opExtrude","SWEPT_FACE",FACE,{"disambiguationData":[OSD([sQuery(id+"F20.wireOp",EDGE,"E69")])]});var subQ1=makeQuery(id+"F7.opExtrude","SWEPT_FACE",FACE,{"disambiguationData":[OSD([sQuery(id+"F5.wireOp",EDGE,"E61")])]});var subQ2=sQuery(id+"F12.wireOp",EDGE,"E64");var subQ3=makeQuery(id+"F13.opExtrude","SWEPT_FACE",FACE,{"disambiguationData":[OSD([subQ2])]});Q1=makeQuery(id+"F25.opFillet","BLEND_EDGE",EDGE,{"blendedFrom":[makeQuery(id+"F21.boolean.opBoolean","SPLIT",EDGE,{"disambiguationData":[TD([makeQuery(id+"F13.boolean.opBoolean","COPY",FACE,{"derivedFrom":makeQuery(id+"F13.opExtrude","CAP_FACE",FACE,{"disambiguationData":[OSD([subQ2])],"isStart":false})})])],"derivedFrom":makeQuery(id+"F13.boolean.opBoolean","INTERSECT",EDGE,{"disambiguationData":[OD(0.0)],"derivedFrom":[subQ1,subQ3]})}),makeQuery(id+"F21.boolean.opBoolean","COPY",FACE,{"derivedFrom":subQ0})],"blendedInto":[makeQuery(id+"F21.boolean.opBoolean","COPY",FACE,{"derivedFrom":subQ0})]});}
            var Q2;
            Q2=makeQuery(id+"F21.boolean.opBoolean","INTERSECT",EDGE,{"derivedFrom":[makeQuery(id+"F7.opExtrude","SWEPT_FACE",FACE,{"disambiguationData":[OSD([sQuery(id+"F5.wireOp",EDGE,"E61")])]}),makeQuery(id+"F21.opExtrude","SWEPT_FACE",FACE,{"disambiguationData":[OSD([sQuery(id+"F20.wireOp",EDGE,"E69")])]})]});
            var Q3;
            Q3=makeQuery(id+"F21.boolean.opBoolean","INTERSECT",EDGE,{"disambiguationData":[OD(1.0)],"derivedFrom":[makeQuery(id+"F13.boolean.opBoolean","COPY",FACE,{"derivedFrom":makeQuery(id+"F13.opExtrude","SWEPT_FACE",FACE,{"disambiguationData":[OSD([sQuery(id+"F12.wireOp",EDGE,"E64")])]})}),makeQuery(id+"F21.opExtrude","SWEPT_FACE",FACE,{"disambiguationData":[OSD([sQuery(id+"F20.wireOp",EDGE,"E70")])]})]});
            var Q4;
            Q4=makeQuery(id+"F21.boolean.opBoolean","INTERSECT",EDGE,{"disambiguationData":[OD(1.0)],"derivedFrom":[makeQuery(id+"F13.boolean.opBoolean","COPY",FACE,{"derivedFrom":makeQuery(id+"F13.opExtrude","SWEPT_FACE",FACE,{"disambiguationData":[OSD([sQuery(id+"F12.wireOp",EDGE,"E64")])]})}),makeQuery(id+"F21.opExtrude","SWEPT_FACE",FACE,{"disambiguationData":[OSD([sQuery(id+"F20.wireOp",EDGE,"E69")])]})]});
            fillet(context, id + "F26", {"entities" : qUnion([Q0, Q1, Q2, Q3, Q4]), "radius" : 0.25 * mm, "tangentPropagation" : true, "allowEdgeOverflow" : false});
        }
    });
